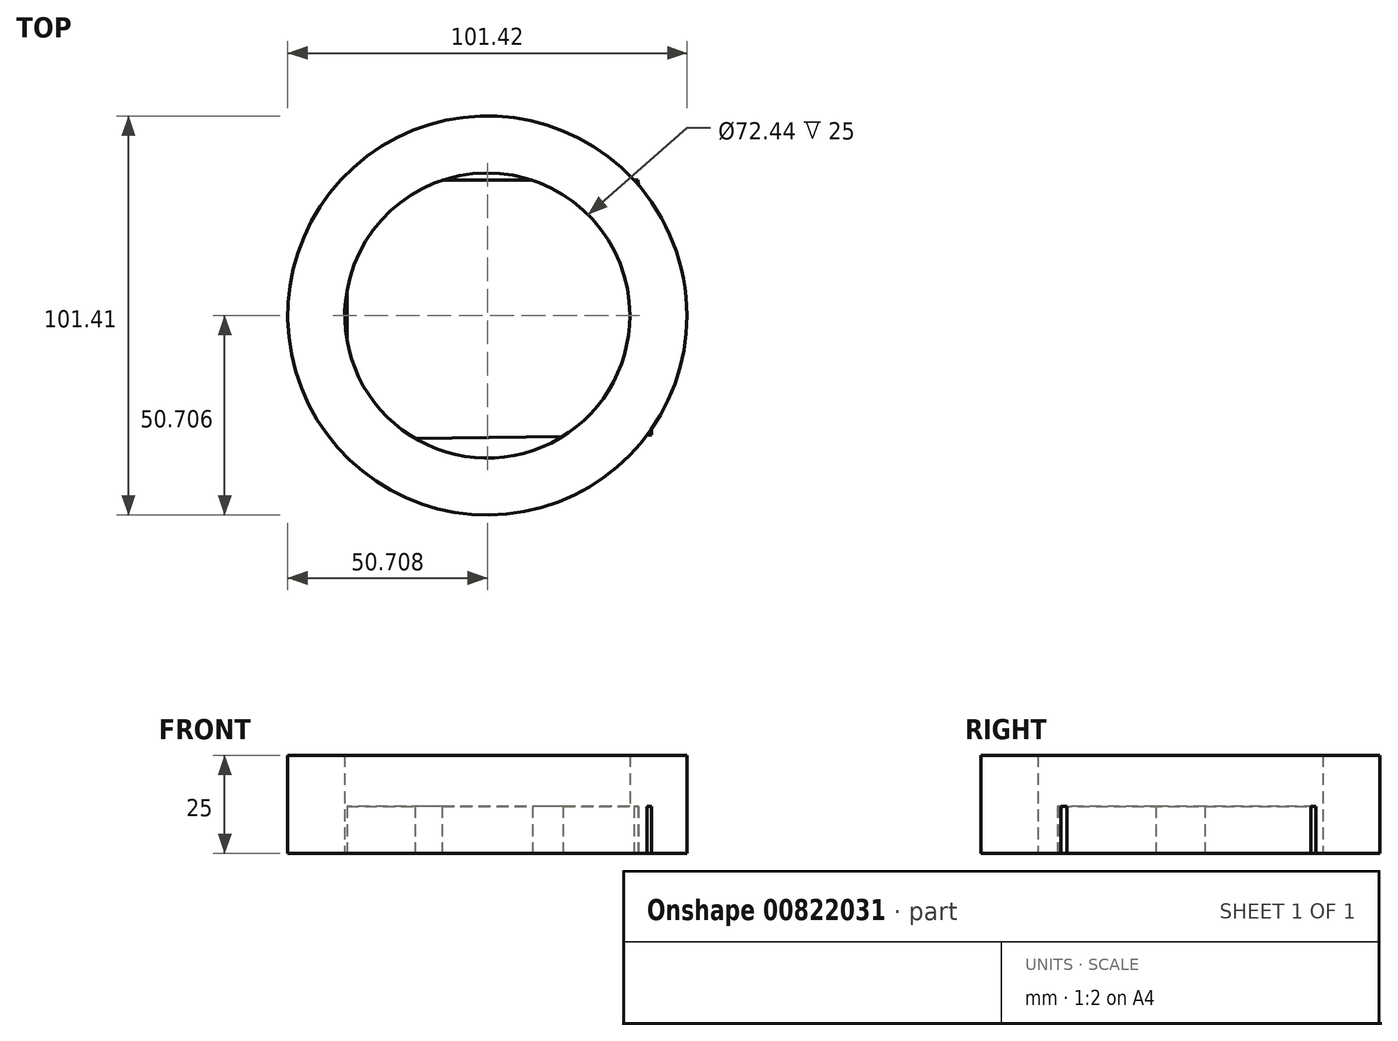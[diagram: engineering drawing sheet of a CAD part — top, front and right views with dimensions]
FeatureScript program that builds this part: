
annotation { "Feature Type Name" : "Feature", "Feature Type Description" : "" }
export const myFeature = defineFeature(function(context is Context, id is Id, definition is map)
    precondition{}
    {
        {
            var Q0;
            Q0=qCreatedBy(makeId("Top.planeOp"),FACE);
            var sketch = newSketch(context, id + "F0", { "sketchPlane" : qUnion([Q0])});
            skLineSegment(sketch, "E0", {"start": v(-39.5, 22.33) * mm, "end": v(-39.5, -43.47) * mm});
            skLineSegment(sketch, "E1", {"start": v(-39.5, -43.47) * mm, "end": v(-39.5, 22.33) * mm});
            skLineSegment(sketch, "E2", {"start": v(-39.5, 22.33) * mm, "end": v(34.49, 22.33) * mm});
            skLineSegment(sketch, "E3", {"start": v(34.49, 22.33) * mm, "end": v(37.92, -42.41) * mm});
            skLineSegment(sketch, "E4", {"start": v(37.92, -42.41) * mm, "end": v(-39.5, -43.47) * mm});
            skSolve(sketch);
        }
        {
            var Q0;
            Q0 = qSketchRegion(id + "F0", true);
            extrude(context, id + "F1", {"entities" : qUnion([Q0]), "depth" : 12 * mm, "offsetDistance" : 25 * mm});
        }
        {
            var Q0;
            Q0=qCreatedBy(makeId("Top.planeOp"),FACE);
            var sketch = newSketch(context, id + "F2", { "sketchPlane" : qUnion([Q0])});
            skCircle(sketch, "E5", {"center": v(-3.83, -12.02) * mm, "radius": 4.87 * mm});
            skCircle(sketch, "E6", {"center": v(-3.83, -12.02) * mm, "radius": 17.05 * mm});
            skCircle(sketch, "E7", {"center": v(-3.83, -12.02) * mm, "radius": 23.29 * mm});
            skCircle(sketch, "E8", {"center": v(-3.83, -12.02) * mm, "radius": 29.53 * mm});
            skCircle(sketch, "E9", {"center": v(-3.83, -12.02) * mm, "radius": 36.22 * mm});
            skCircle(sketch, "E10", {"center": v(-3.83, -12.02) * mm, "radius": 10.61 * mm});
            skCircle(sketch, "E11", {"center": v(-3.83, -12.02) * mm, "radius": 50.7 * mm});
            skSolve(sketch);
        }
        {
            var Q0;
            Q0 = qSketchRegion(id + "F2", true);
            extrude(context, id + "F3", {"entities" : qUnion([Q0]), "operationType" : NewBodyOperationType.ADD, "depth" : 25 * mm, "offsetDistance" : 25 * mm});
        }
    });
